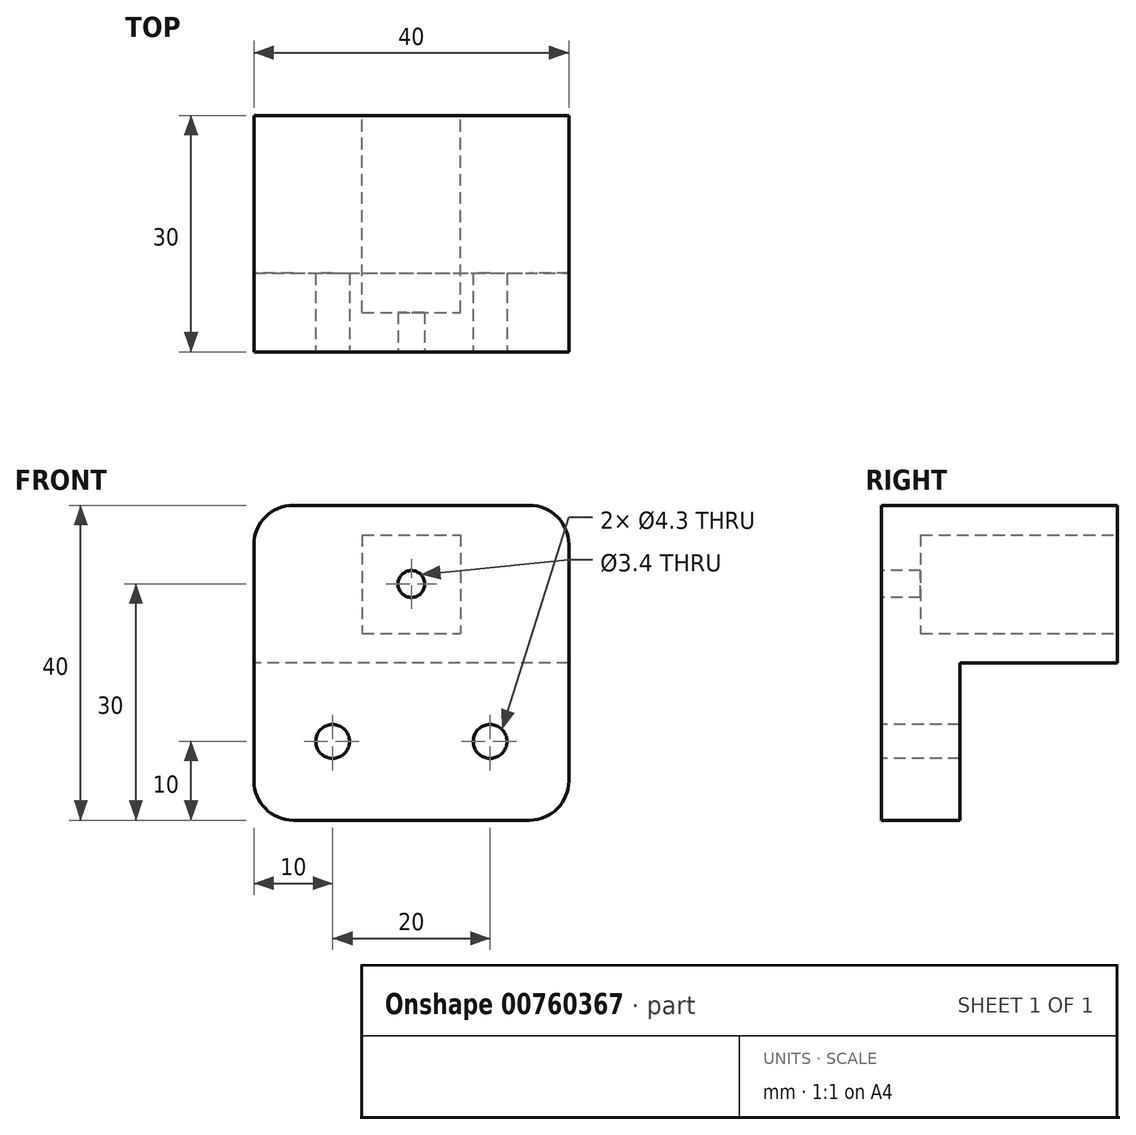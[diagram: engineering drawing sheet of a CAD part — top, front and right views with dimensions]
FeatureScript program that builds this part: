
annotation { "Feature Type Name" : "Feature", "Feature Type Description" : "" }
export const myFeature = defineFeature(function(context is Context, id is Id, definition is map)
    precondition{}
    {
        {
            var Q0;
            Q0=qCreatedBy(makeId("Top.planeOp"),FACE);
            var sketch = newSketch(context, id + "F0", { "sketchPlane" : qUnion([Q0])});
            skLineSegment(sketch, "E0.bottom", {"start": v(20, 15) * mm, "end": v(-20, 15) * mm});
            skLineSegment(sketch, "E0.top", {"start": v(20, -15) * mm, "end": v(-20, -15) * mm});
            skLineSegment(sketch, "E0.left", {"start": v(20, 15) * mm, "end": v(20, -15) * mm});
            skLineSegment(sketch, "E0.right", {"start": v(-20, 15) * mm, "end": v(-20, -15) * mm});
            skPoint(sketch, "E0.middle", {"position": v(0, 0) * mm});
            skLineSegment(sketch, "E1", {"start": v(-20, -5) * mm, "end": v(20, -5) * mm});
            skSolve(sketch);
        }
        {
            var Q0;
            Q0=qSketchRegion(id+"F0",true);
            extrude(context, id + "F1", {"entities" : qUnion([Q0]), "depth" : 40 * mm});
        }
        {
            var Q0;
            {var subQ0=sQuery(id+"F0.wireOp",EDGE,"E0.bottom");Q0=makeQuery(id+"F0.imprint","IMPRINT",FACE,{"disambiguationData":[TD([[makeQuery(id+"F0.imprint","IMPRINT",EDGE,{"derivedFrom":subQ0}),1.0]])]});}
            extrude(context, id + "F2", {"entities" : qUnion([Q0]), "operationType" : NewBodyOperationType.REMOVE, "depth" : 20 * mm});
        }
        {
            var Q0;
            Q0=makeQuery(id+"F1.opExtrude","SWEPT_FACE",FACE,{"disambiguationData":[OSD([sQuery(id+"F0.wireOp",EDGE,"E0.top")])]});
            var sketch = newSketch(context, id + "F3", { "sketchPlane" : qUnion([Q0])});
            skCircle(sketch, "E2", {"center": v(-10, 10) * mm, "radius": 2.15 * mm});
            skCircle(sketch, "E3", {"center": v(10, 10) * mm, "radius": 2.15 * mm});
            skCircle(sketch, "E4", {"center": v(0, 30) * mm, "radius": 1.7 * mm});
            skSolve(sketch);
        }
        {
            var Q0;
            Q0=qSketchRegion(id+"F3",true);
            extrude(context, id + "F4", {"entities" : qUnion([Q0]), "operationType" : NewBodyOperationType.REMOVE, "oppositeDirection" : true, "depth" : 40 * mm});
        }
        {
            var Q0;
            Q0=makeQuery(id+"F1.opExtrude","SWEPT_FACE",FACE,{"disambiguationData":[OSD([sQuery(id+"F0.wireOp",EDGE,"E0.bottom")])]});
            var sketch = newSketch(context, id + "F5", { "sketchPlane" : qUnion([Q0])});
            skLineSegment(sketch, "E5.bottom", {"start": v(6.25, 36.25) * mm, "end": v(-6.25, 36.25) * mm});
            skLineSegment(sketch, "E5.top", {"start": v(6.25, 23.75) * mm, "end": v(-6.25, 23.75) * mm});
            skLineSegment(sketch, "E5.left", {"start": v(6.25, 36.25) * mm, "end": v(6.25, 23.75) * mm});
            skLineSegment(sketch, "E5.right", {"start": v(-6.25, 36.25) * mm, "end": v(-6.25, 23.75) * mm});
            skPoint(sketch, "E5.middle", {"position": v(0, 30) * mm});
            skSolve(sketch);
        }
        {
            var Q0;
            Q0=makeQuery(id+"F5.imprint","IMPRINT",FACE,{"disambiguationData":[TD([[makeQuery(id+"F5.imprint","IMPRINT",EDGE,{"derivedFrom":sQuery(id+"F5.wireOp",EDGE,"E5.bottom")}),1.0]])]});
            extrude(context, id + "F6", {"entities" : qUnion([Q0]), "operationType" : NewBodyOperationType.REMOVE, "oppositeDirection" : true, "depth" : 25 * mm});
        }
        {
            var Q0;
            Q0=makeQuery(id+"F1.opExtrude","CAP_EDGE",EDGE,{"disambiguationData":[OSD([sQuery(id+"F0.wireOp",EDGE,"E0.right")])],"isStart":true});
            var Q1;
            Q1=makeQuery(id+"F1.opExtrude","CAP_EDGE",EDGE,{"disambiguationData":[OSD([sQuery(id+"F0.wireOp",EDGE,"E0.left")])],"isStart":true});
            var Q2;
            Q2=makeQuery(id+"F1.opExtrude","CAP_EDGE",EDGE,{"disambiguationData":[OSD([sQuery(id+"F0.wireOp",EDGE,"E0.right")])],"isStart":false});
            var Q3;
            Q3=makeQuery(id+"F1.opExtrude","CAP_EDGE",EDGE,{"disambiguationData":[OSD([sQuery(id+"F0.wireOp",EDGE,"E0.left")])],"isStart":false});
            fillet(context, id + "F7", {"entities" : qUnion([Q0, Q1, Q2, Q3]), "radius" : 5 * mm, "tangentPropagation" : true, "allowEdgeOverflow" : false});
        }
    });
